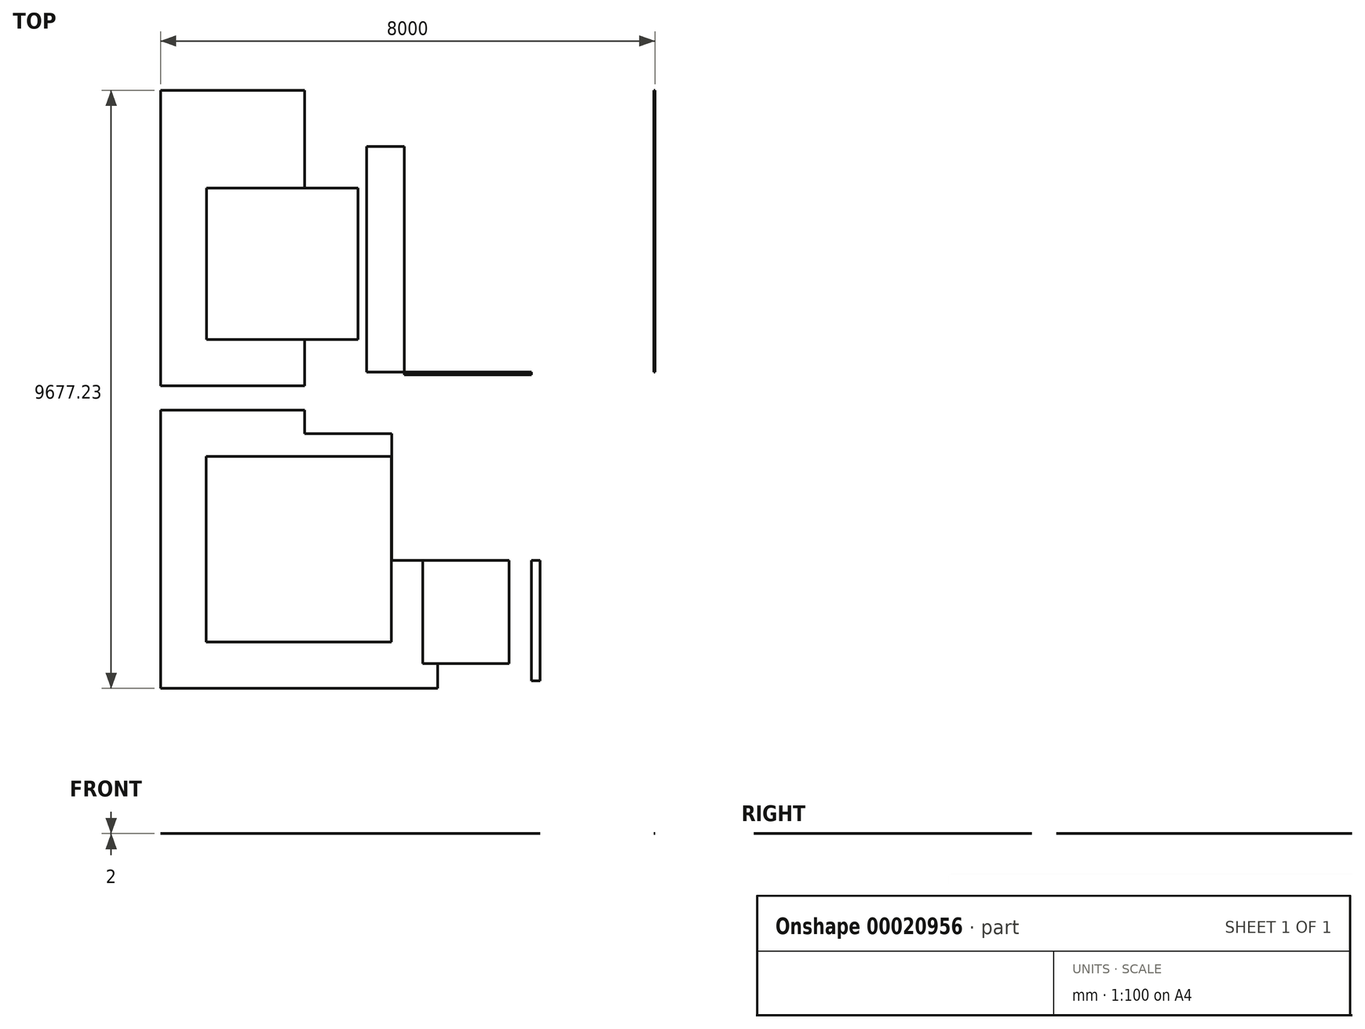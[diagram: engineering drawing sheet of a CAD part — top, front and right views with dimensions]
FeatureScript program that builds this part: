
annotation { "Feature Type Name" : "Feature", "Feature Type Description" : "" }
export const myFeature = defineFeature(function(context is Context, id is Id, definition is map)
    precondition{}
    {
        {
            var Q0;
            Q0=qCreatedBy(makeId("Top.planeOp"),FACE);
            var sketch = newSketch(context, id + "F0", { "sketchPlane" : qUnion([Q0])});
            skLineSegment(sketch, "E0.bottom", {"start": v(-8000, 9700) * mm, "end": v(0, 9700) * mm});
            skLineSegment(sketch, "E0.top", {"start": v(-8000, 0) * mm, "end": v(0, 0) * mm});
            skLineSegment(sketch, "E0.left", {"start": v(-8000, 9700) * mm, "end": v(-8000, 0) * mm});
            skLineSegment(sketch, "E0.right", {"start": v(0, 9700) * mm, "end": v(0, 0) * mm});
            skLineSegment(sketch, "E1.bottom", {"start": v(-2000, 142.21) * mm, "end": v(0, 142.21) * mm});
            skLineSegment(sketch, "E1.top", {"start": v(-2000, 5142.21) * mm, "end": v(0, 5142.21) * mm});
            skLineSegment(sketch, "E1.left", {"start": v(-2000, 142.21) * mm, "end": v(-2000, 5142.21) * mm});
            skLineSegment(sketch, "E1.right", {"start": v(0, 142.21) * mm, "end": v(0, 5142.21) * mm});
            skLineSegment(sketch, "E2.bottom", {"start": v(-4666, 5142.21) * mm, "end": v(-1016, 5142.21) * mm});
            skLineSegment(sketch, "E2.top", {"start": v(-4666, 8792.21) * mm, "end": v(-1016, 8792.21) * mm});
            skLineSegment(sketch, "E2.left", {"start": v(-4666, 5142.21) * mm, "end": v(-4666, 8792.21) * mm});
            skLineSegment(sketch, "E2.right", {"start": v(-1016, 5142.21) * mm, "end": v(-1016, 8792.21) * mm});
            skLineSegment(sketch, "E3.0", {"start": v(-5666, 4142.21) * mm, "end": v(-5666, 9792.21) * mm});
            skLineSegment(sketch, "E3.1", {"start": v(-5666, 4142.21) * mm, "end": v(-16, 4142.21) * mm});
            skLineSegment(sketch, "E3.2", {"start": v(-16, 4142.21) * mm, "end": v(-16, 9792.21) * mm});
            skLineSegment(sketch, "E3.3", {"start": v(-5666, 9792.21) * mm, "end": v(-16, 9792.21) * mm});
            skLineSegment(sketch, "E4.bottom", {"start": v(-3758.67, 424.98) * mm, "end": v(-2358.67, 424.98) * mm});
            skLineSegment(sketch, "E4.top", {"start": v(-3758.67, 2424.98) * mm, "end": v(-2358.67, 2424.98) * mm});
            skLineSegment(sketch, "E4.left", {"start": v(-3758.67, 424.98) * mm, "end": v(-3758.67, 2424.98) * mm});
            skLineSegment(sketch, "E4.right", {"start": v(-2358.67, 424.98) * mm, "end": v(-2358.67, 2424.98) * mm});
            skLineSegment(sketch, "E5.0", {"start": v(-4258.67, -75.02) * mm, "end": v(-4258.67, 2924.98) * mm});
            skLineSegment(sketch, "E5.1", {"start": v(-4258.67, -75.02) * mm, "end": v(-1858.67, -75.02) * mm});
            skLineSegment(sketch, "E5.2", {"start": v(-1858.67, -75.02) * mm, "end": v(-1858.67, 2924.98) * mm});
            skLineSegment(sketch, "E5.3", {"start": v(-4258.67, 2924.98) * mm, "end": v(-1858.67, 2924.98) * mm});
            skPoint(sketch, "E6.firstSnap0", {"position": v(-1858.67, 1424.98) * mm});
            skLineSegment(sketch, "E6.bottom", {"start": v(-7254.58, 5668.85) * mm, "end": v(-4804.58, 5668.85) * mm});
            skLineSegment(sketch, "E6.top", {"start": v(-7254.58, 8118.85) * mm, "end": v(-4804.58, 8118.85) * mm});
            skLineSegment(sketch, "E6.left", {"start": v(-7254.58, 5668.85) * mm, "end": v(-7254.58, 8118.85) * mm});
            skLineSegment(sketch, "E6.right", {"start": v(-4804.58, 5668.85) * mm, "end": v(-4804.58, 8118.85) * mm});
            skLineSegment(sketch, "E7.0", {"start": v(-8004.58, 4918.85) * mm, "end": v(-8004.58, 8868.85) * mm});
            skLineSegment(sketch, "E7.1", {"start": v(-8004.58, 4918.85) * mm, "end": v(-4054.58, 4918.85) * mm});
            skLineSegment(sketch, "E7.2", {"start": v(-4054.58, 4918.85) * mm, "end": v(-4054.58, 8868.85) * mm});
            skLineSegment(sketch, "E7.3", {"start": v(-8004.58, 8868.85) * mm, "end": v(-4054.58, 8868.85) * mm});
            skLineSegment(sketch, "E8.bottom", {"start": v(-7264.8, 3772.77) * mm, "end": v(-4264.8, 3772.77) * mm});
            skLineSegment(sketch, "E8.top", {"start": v(-7264.8, 772.77) * mm, "end": v(-4264.8, 772.77) * mm});
            skLineSegment(sketch, "E8.left", {"start": v(-7264.8, 3772.77) * mm, "end": v(-7264.8, 772.77) * mm});
            skLineSegment(sketch, "E8.right", {"start": v(-4264.8, 3772.77) * mm, "end": v(-4264.8, 772.77) * mm});
            skLineSegment(sketch, "E9.0", {"start": v(-8014.8, 4522.77) * mm, "end": v(-3514.8, 4522.77) * mm});
            skLineSegment(sketch, "E9.1", {"start": v(-8014.8, 4522.77) * mm, "end": v(-8014.8, 22.77) * mm});
            skLineSegment(sketch, "E9.2", {"start": v(-8014.8, 22.77) * mm, "end": v(-3514.8, 22.77) * mm});
            skLineSegment(sketch, "E9.3", {"start": v(-3514.8, 4522.77) * mm, "end": v(-3514.8, 22.77) * mm});
            skLineSegment(sketch, "E10.bottom", {"start": v(-12940.47, 11263.4) * mm, "end": v(-11240.47, 11263.4) * mm});
            skLineSegment(sketch, "E10.top", {"start": v(-12940.47, 8863.4) * mm, "end": v(-11240.47, 8863.4) * mm});
            skLineSegment(sketch, "E10.left", {"start": v(-12940.47, 11263.4) * mm, "end": v(-12940.47, 8863.4) * mm});
            skLineSegment(sketch, "E10.right", {"start": v(-11240.47, 11263.4) * mm, "end": v(-11240.47, 8863.4) * mm});
            skLineSegment(sketch, "E11.0", {"start": v(-13440.47, 11763.4) * mm, "end": v(-10740.47, 11763.4) * mm});
            skLineSegment(sketch, "E11.1", {"start": v(-13440.47, 11763.4) * mm, "end": v(-13440.47, 8363.4) * mm});
            skLineSegment(sketch, "E11.2", {"start": v(-13440.47, 8363.4) * mm, "end": v(-10740.47, 8363.4) * mm});
            skLineSegment(sketch, "E11.3", {"start": v(-10740.47, 11763.4) * mm, "end": v(-10740.47, 8363.4) * mm});
            skLineSegment(sketch, "E12.bottom", {"start": v(-3758.67, 2594.86) * mm, "end": v(-2358.67, 2594.86) * mm});
            skLineSegment(sketch, "E12.top", {"start": v(-3758.67, 4594.86) * mm, "end": v(-2358.67, 4594.86) * mm});
            skLineSegment(sketch, "E12.left", {"start": v(-3758.67, 2594.86) * mm, "end": v(-3758.67, 4594.86) * mm});
            skLineSegment(sketch, "E12.right", {"start": v(-2358.67, 2594.86) * mm, "end": v(-2358.67, 4594.86) * mm});
            skLineSegment(sketch, "E13.0", {"start": v(-4258.67, 2094.86) * mm, "end": v(-4258.67, 5094.86) * mm});
            skLineSegment(sketch, "E13.1", {"start": v(-4258.67, 2094.86) * mm, "end": v(-1858.67, 2094.86) * mm});
            skLineSegment(sketch, "E13.2", {"start": v(-1858.67, 2094.86) * mm, "end": v(-1858.67, 5094.86) * mm});
            skLineSegment(sketch, "E13.3", {"start": v(-4258.67, 5094.86) * mm, "end": v(-1858.67, 5094.86) * mm});
            skSolve(sketch);
        }
        {
            var Q0;
            Q0=makeQuery(id+"F0.imprint","IMPRINT",FACE,{"disambiguationData":[TD([[makeQuery(id+"F0.imprint","IMPRINT",EDGE,{"derivedFrom":sQuery(id+"F0.wireOp",EDGE,"E0.bottom")}),-1.0]])]});
            var Q1;
            Q1=makeQuery(id+"F0.imprint","IMPRINT",FACE,{"disambiguationData":[TD([[makeQuery(id+"F0.imprint","IMPRINT",EDGE,{"derivedFrom":sQuery(id+"F0.wireOp",EDGE,"E4.bottom")}),-1.0]])]});
            var Q2;
            Q2=makeQuery(id+"F0.imprint","IMPRINT",FACE,{"disambiguationData":[TD([[makeQuery(id+"F0.imprint","IMPRINT",EDGE,{"derivedFrom":sQuery(id+"F0.wireOp",EDGE,"E6.bottom")}),-1.0]])]});
            var Q3;
            Q3=makeQuery(id+"F0.imprint","IMPRINT",FACE,{"disambiguationData":[TD([[makeQuery(id+"F0.imprint","IMPRINT",EDGE,{"derivedFrom":sQuery(id+"F0.wireOp",EDGE,"E2.bottom")}),-1.0]])]});
            var Q4;
            Q4=makeQuery(id+"F0.imprint","IMPRINT",FACE,{"disambiguationData":[TD([[makeQuery(id+"F0.imprint","IMPRINT",EDGE,{"derivedFrom":sQuery(id+"F0.wireOp",EDGE,"E4.bottom")}),1.0]])]});
            var Q5;
            Q5=makeQuery(id+"F0.imprint","IMPRINT",FACE,{"disambiguationData":[TD([[makeQuery(id+"F0.imprint","IMPRINT",EDGE,{"derivedFrom":sQuery(id+"F0.wireOp",EDGE,"E6.bottom")}),1.0]])]});
            var Q6;
            Q6=makeQuery(id+"F0.imprint","IMPRINT",FACE,{"disambiguationData":[TD([[makeQuery(id+"F0.imprint","IMPRINT",EDGE,{"derivedFrom":sQuery(id+"F0.wireOp",EDGE,"E2.bottom")}),1.0]])]});
            var Q7;
            Q7=makeQuery(id+"F0.imprint","IMPRINT",FACE,{"disambiguationData":[TD([[makeQuery(id+"F0.imprint","IMPRINT",EDGE,{"derivedFrom":sQuery(id+"F0.wireOp",EDGE,"E1.bottom")}),1.0]])]});
            var Q8;
            Q8=makeQuery(id+"F0.imprint","IMPRINT",FACE,{"disambiguationData":[TD([[makeQuery(id+"F0.imprint","IMPRINT",EDGE,{"derivedFrom":sQuery(id+"F0.wireOp",EDGE,"E8.bottom")}),1.0]])]});
            var Q9;
            Q9=makeQuery(id+"F0.imprint","IMPRINT",FACE,{"disambiguationData":[TD([[makeQuery(id+"F0.imprint","IMPRINT",EDGE,{"derivedFrom":sQuery(id+"F0.wireOp",EDGE,"E8.bottom")}),-1.0]])]});
            extrude(context, id + "F1", {"entities" : qUnion([Q0, Q1, Q2, Q3, Q4, Q5, Q6, Q7, Q8, Q9]), "depth" : 1 * mm, "offsetDistance" : 25 * mm});
        }
        {
            var Q0;
            Q0=makeQuery(id+"F0.imprint","IMPRINT",FACE,{"disambiguationData":[TD([[makeQuery(id+"F0.imprint","IMPRINT",EDGE,{"derivedFrom":sQuery(id+"F0.wireOp",EDGE,"E4.bottom")}),1.0]])]});
            var Q1;
            Q1=makeQuery(id+"F0.imprint","IMPRINT",FACE,{"disambiguationData":[TD([[makeQuery(id+"F0.imprint","IMPRINT",EDGE,{"derivedFrom":sQuery(id+"F0.wireOp",EDGE,"E6.bottom")}),1.0]])]});
            var Q2;
            Q2=makeQuery(id+"F0.imprint","IMPRINT",FACE,{"disambiguationData":[TD([[makeQuery(id+"F0.imprint","IMPRINT",EDGE,{"derivedFrom":sQuery(id+"F0.wireOp",EDGE,"E2.bottom")}),1.0]])]});
            var Q3;
            Q3=makeQuery(id+"F0.imprint","IMPRINT",FACE,{"disambiguationData":[TD([[makeQuery(id+"F0.imprint","IMPRINT",EDGE,{"derivedFrom":sQuery(id+"F0.wireOp",EDGE,"E8.bottom")}),-1.0]])]});
            extrude(context, id + "F2", {"entities" : qUnion([Q0, Q1, Q2, Q3]), "operationType" : NewBodyOperationType.ADD, "depth" : 2 * mm, "offsetDistance" : 25 * mm});
        }
    });
